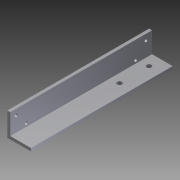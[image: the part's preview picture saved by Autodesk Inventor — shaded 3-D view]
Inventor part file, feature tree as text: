
AUTODESK INVENTOR PART (.ipt)
format: ipt  version: 2012 (Build 160160000, 160)  size: 86,528 bytes
history: native  units: in
note: dims shown in document units (in); Inventor stores cm internally (conversion verified against a paired STEP export)
features: other x3, sketch x1
ambient origin geometry x8: Origin, YZ Plane, XZ Plane, XY Plane, X Axis, Y Axis, Z Axis, Center Point
bodies: Solid1 (feature_tree)
feature tree (4):
  other  "8 ball corner L.ipt"
  other  "Solid1::8 ball corner L.ipt"
  sketch  "Sketch1"  dims[d0=0.3937in]
  other  "TaggingFeature1"
